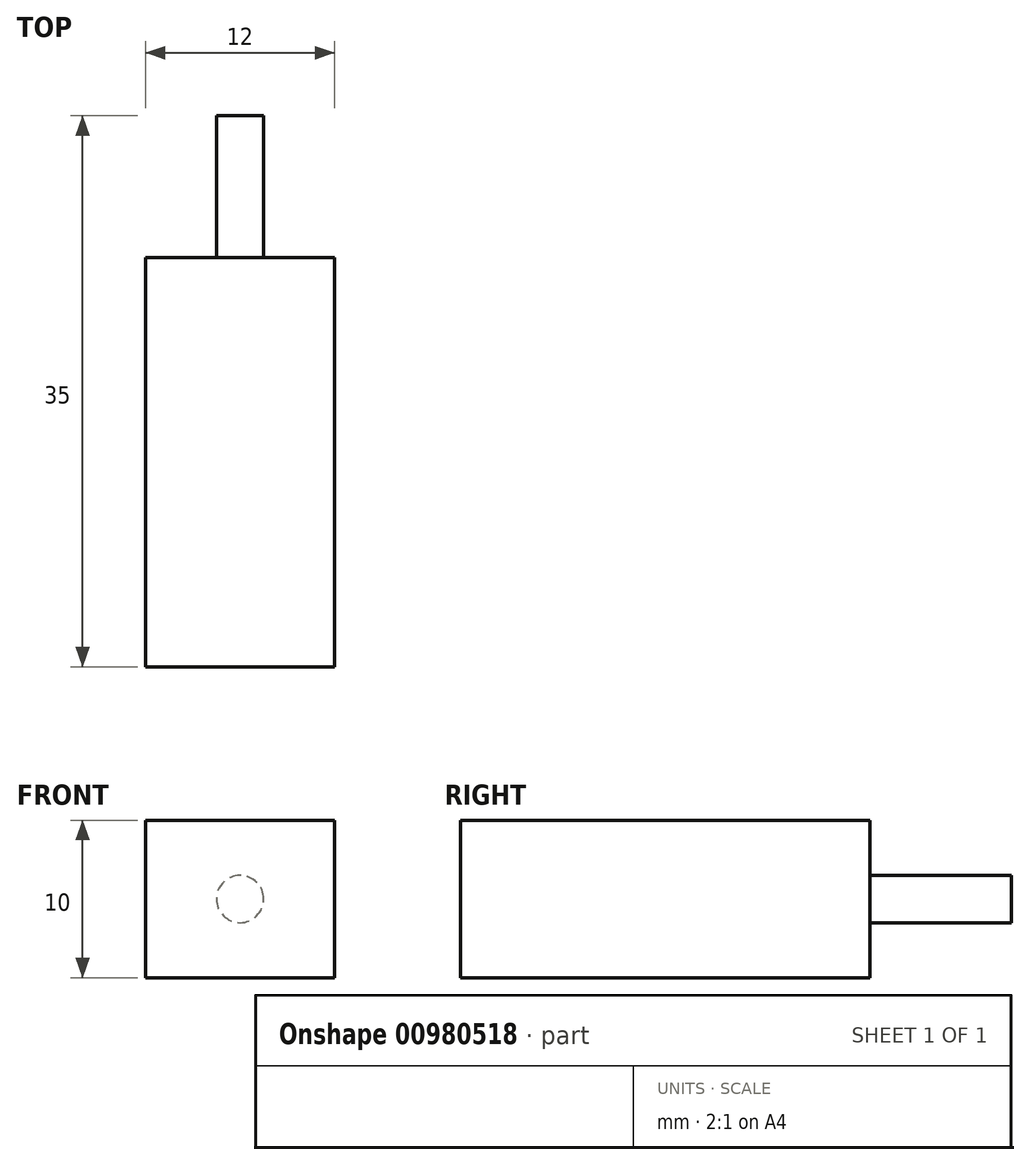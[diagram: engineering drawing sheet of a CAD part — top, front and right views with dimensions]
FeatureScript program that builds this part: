
annotation { "Feature Type Name" : "Feature", "Feature Type Description" : "" }
export const myFeature = defineFeature(function(context is Context, id is Id, definition is map)
    precondition{}
    {
        {
            var Q0;
            Q0=qCreatedBy(makeId("Front.planeOp"),FACE);
            var sketch = newSketch(context, id + "F0", { "sketchPlane" : qUnion([Q0])});
            skLineSegment(sketch, "E0.bottom", {"start": v(-6, 5) * mm, "end": v(6, 5) * mm});
            skLineSegment(sketch, "E0.top", {"start": v(-6, -5) * mm, "end": v(6, -5) * mm});
            skLineSegment(sketch, "E0.left", {"start": v(-6, 5) * mm, "end": v(-6, -5) * mm});
            skLineSegment(sketch, "E0.right", {"start": v(6, 5) * mm, "end": v(6, -5) * mm});
            skPoint(sketch, "E1", {"position": v(0, 5) * mm});
            skPoint(sketch, "E2", {"position": v(-6, 0) * mm});
            skSolve(sketch);
        }
        {
            var Q0;
            Q0=makeQuery(id+"F0.imprint","IMPRINT",FACE,{"disambiguationData":[TD([[makeQuery(id+"F0.imprint","IMPRINT",EDGE,{"derivedFrom":sQuery(id+"F0.wireOp",EDGE,"E0.bottom")}),-1.0]])]});
            extrude(context, id + "F1", {"entities" : qUnion([Q0]), "depth" : 26 * mm, "offsetDistance" : 25.4 * mm});
        }
        {
            var Q0;
            Q0=makeQuery(id+"F1.opExtrude","CAP_FACE",FACE,{"disambiguationData":[OSD([sQuery(id+"F0.wireOp",EDGE,"E0.bottom"),sQuery(id+"F0.wireOp",EDGE,"E0.top"),sQuery(id+"F0.wireOp",EDGE,"E0.left"),sQuery(id+"F0.wireOp",EDGE,"E0.right")])],"isStart":true});
            var sketch = newSketch(context, id + "F2", { "sketchPlane" : qUnion([Q0])});
            skCircle(sketch, "E3", {"center": v(0, 0) * mm, "radius": 1.5 * mm});
            skSolve(sketch);
        }
        {
            var Q0;
            Q0=makeQuery(id+"F2.imprint","IMPRINT",FACE,{"disambiguationData":[TD([[makeQuery(id+"F2.imprint","IMPRINT",EDGE,{"derivedFrom":sQuery(id+"F2.wireOp",EDGE,"E3")}),1.0]])]});
            extrude(context, id + "F3", {"entities" : qUnion([Q0]), "operationType" : NewBodyOperationType.ADD, "depth" : 9 * mm, "offsetDistance" : 25.4 * mm});
        }
    });
